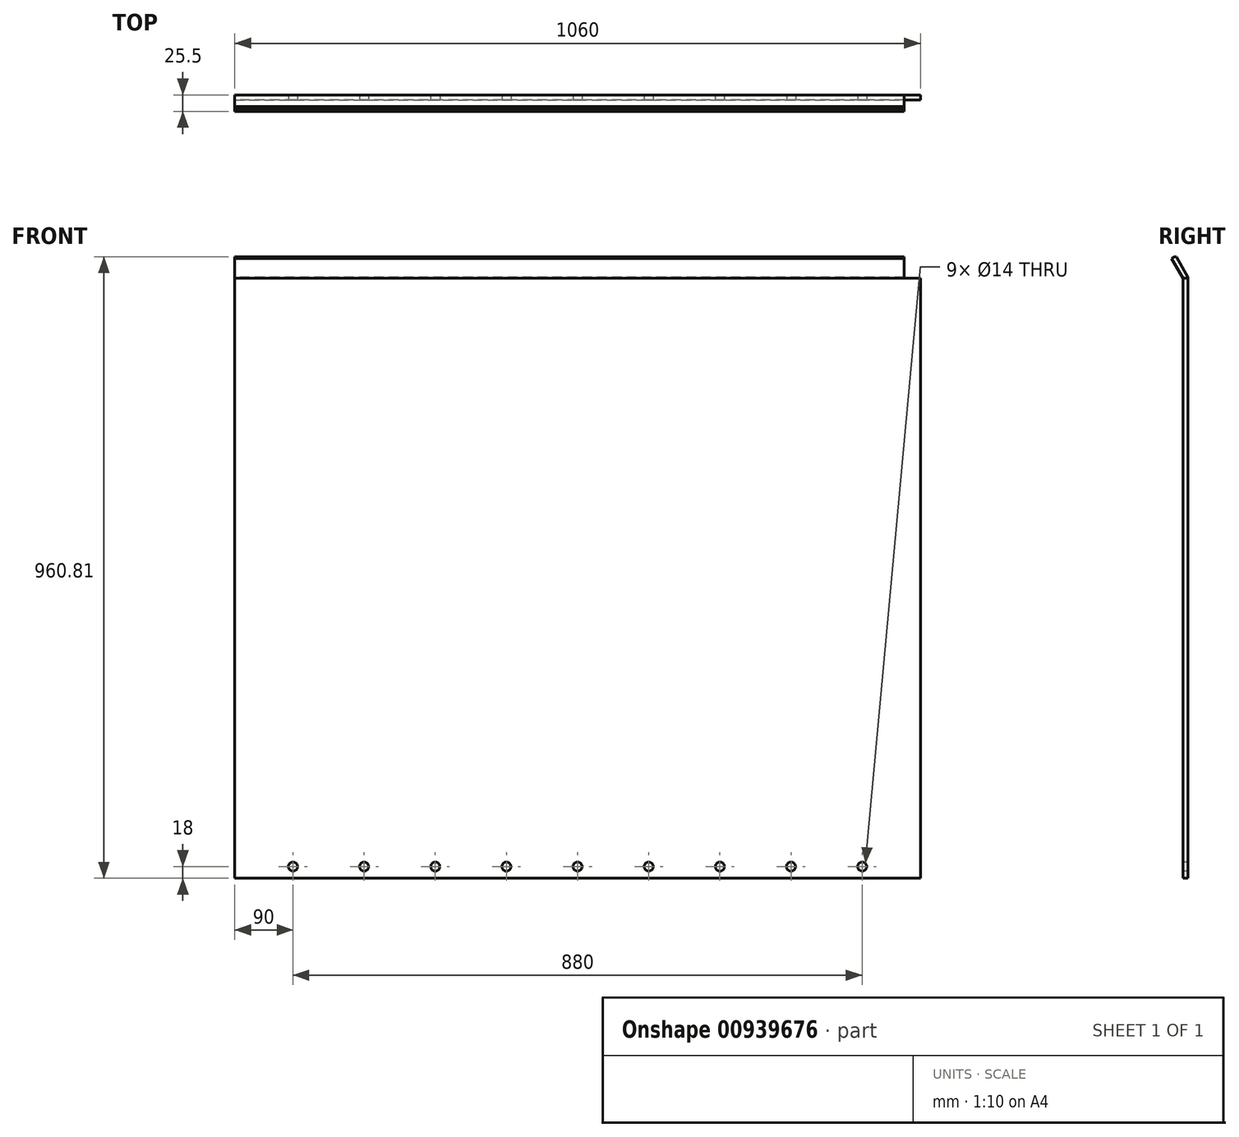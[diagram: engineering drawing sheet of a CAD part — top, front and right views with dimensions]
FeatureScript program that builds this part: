
annotation { "Feature Type Name" : "Feature", "Feature Type Description" : "" }
export const myFeature = defineFeature(function(context is Context, id is Id, definition is map)
    precondition{}
    {
        {
            var Q0;
            Q0=qCreatedBy(makeId("Right.planeOp"),FACE);
            var sketch = newSketch(context, id + "F0", { "sketchPlane" : qUnion([Q0])});
            skLineSegment(sketch, "E0", {"start": v(0, 0) * mm, "end": v(0, 940) * mm});
            skLineSegment(sketch, "E1", {"start": v(0, 0) * mm, "end": v(-6.47, -24.15) * mm});
            skLineSegment(sketch, "E2", {"start": v(0, 940) * mm, "end": v(-17.5, 970.31) * mm});
            skLineSegment(sketch, "E3.0", {"start": v(5, -0.66) * mm, "end": v(-1.64, -25.44) * mm});
            skLineSegment(sketch, "E3.1", {"start": v(5, -0.66) * mm, "end": v(5, 941.34) * mm});
            skLineSegment(sketch, "E3.2", {"start": v(5, 941.34) * mm, "end": v(-13.17, 972.81) * mm});
            skLineSegment(sketch, "E4", {"start": v(-1.64, -25.44) * mm, "end": v(-6.47, -24.15) * mm});
            skLineSegment(sketch, "E5", {"start": v(-13.17, 972.81) * mm, "end": v(-17.5, 970.31) * mm});
            skSolve(sketch);
        }
        {
            var Q0;
            Q0=makeQuery(id+"F0.imprint","IMPRINT",FACE,{"disambiguationData":[TD([[makeQuery(id+"F0.imprint","IMPRINT",EDGE,{"derivedFrom":sQuery(id+"F0.wireOp",EDGE,"E0")}),-1.0]])]});
            extrude(context, id + "F1", {"entities" : qUnion([Q0]), "endBound" : BoundingType.SYMMETRIC, "depth" : 1060 * mm, "offsetDistance" : 25 * mm});
        }
        {
            var Q0;
            Q0=makeQuery(id+"F1.opExtrude","CAP_FACE",FACE,{"disambiguationData":[OSD([sQuery(id+"F0.wireOp",EDGE,"E0"),sQuery(id+"F0.wireOp",EDGE,"E1"),sQuery(id+"F0.wireOp",EDGE,"E2"),sQuery(id+"F0.wireOp",EDGE,"E3.0"),sQuery(id+"F0.wireOp",EDGE,"E3.1"),sQuery(id+"F0.wireOp",EDGE,"E3.2"),sQuery(id+"F0.wireOp",EDGE,"E4"),sQuery(id+"F0.wireOp",EDGE,"E5")])],"isStart":false});
            var sketch = newSketch(context, id + "F2", { "sketchPlane" : qUnion([Q0])});
            skLineSegment(sketch, "E6", {"start": v(0, 940) * mm, "end": v(5, 940) * mm});
            skLineSegment(sketch, "E7", {"start": v(5, 940) * mm, "end": v(5, 941.34) * mm});
            skLineSegment(sketch, "E8", {"start": v(5, 941.34) * mm, "end": v(-13.17, 972.81) * mm});
            skLineSegment(sketch, "E9", {"start": v(-13.17, 972.81) * mm, "end": v(-17.5, 970.31) * mm});
            skLineSegment(sketch, "E10", {"start": v(-17.5, 970.31) * mm, "end": v(0, 940) * mm});
            skLineSegment(sketch, "E11", {"start": v(-6.47, -24.15) * mm, "end": v(-1.64, -25.44) * mm});
            skLineSegment(sketch, "E12", {"start": v(-1.64, -25.44) * mm, "end": v(5, -0.66) * mm});
            skLineSegment(sketch, "E13", {"start": v(5, -0.66) * mm, "end": v(5, 0) * mm});
            skLineSegment(sketch, "E14", {"start": v(5, 0) * mm, "end": v(0, 0) * mm});
            skLineSegment(sketch, "E15", {"start": v(0, 0) * mm, "end": v(-6.47, -24.15) * mm});
            skSolve(sketch);
        }
        {
            var Q0;
            Q0=makeQuery(id+"F2.imprint","IMPRINT",FACE,{"disambiguationData":[TD([[makeQuery(id+"F2.imprint","IMPRINT",EDGE,{"derivedFrom":sQuery(id+"F2.wireOp",EDGE,"E11")}),-1.0]])]});
            var Q1;
            Q1=makeQuery(id+"F2.imprint","IMPRINT",FACE,{"disambiguationData":[TD([[makeQuery(id+"F2.imprint","IMPRINT",EDGE,{"derivedFrom":sQuery(id+"F2.wireOp",EDGE,"E6")}),1.0]])]});
            extrude(context, id + "F3", {"entities" : qUnion([Q0, Q1]), "operationType" : NewBodyOperationType.REMOVE, "oppositeDirection" : true, "depth" : 25 * mm, "offsetDistance" : 25 * mm});
        }
        {
            var Q0;
            Q0=makeQuery(id+"F1.opExtrude","SWEPT_FACE",FACE,{"disambiguationData":[OSD([sQuery(id+"F0.wireOp",EDGE,"E0")])]});
            var sketch = newSketch(context, id + "F4", { "sketchPlane" : qUnion([Q0])});
            skCircle(sketch, "E16", {"center": v(0, 30) * mm, "radius": 7 * mm});
            skCircle(sketch, "E17.1.0.0", {"center": v(110, 30) * mm, "radius": 7 * mm});
            skCircle(sketch, "E17.2.0.0", {"center": v(220, 30) * mm, "radius": 7 * mm});
            skCircle(sketch, "E17.3.0.0", {"center": v(330, 30) * mm, "radius": 7 * mm});
            skCircle(sketch, "E17.4.0.0", {"center": v(440, 30) * mm, "radius": 7 * mm});
            skLineSegment(sketch, "E17.direction1", {"start": v(0, 30) * mm, "end": v(110, 30) * mm, "construction": true});
            skCircle(sketch, "E18.MirrorC", {"center": v(-110, 30) * mm, "radius": 7 * mm});
            skCircle(sketch, "E19.MirrorC", {"center": v(-220, 30) * mm, "radius": 7 * mm});
            skCircle(sketch, "E20.MirrorC", {"center": v(-330, 30) * mm, "radius": 7 * mm});
            skCircle(sketch, "E21.MirrorC", {"center": v(-440, 30) * mm, "radius": 7 * mm});
            skSolve(sketch);
        }
        {
            var Q0;
            Q0=qSketchRegion(id+"F4",true);
            extrude(context, id + "F5", {"entities" : qUnion([Q0]), "operationType" : NewBodyOperationType.REMOVE, "endBound" : BoundingType.THROUGH_ALL, "oppositeDirection" : true, "depth" : 25 * mm, "offsetDistance" : 25 * mm});
        }
        {
            var Q0;
            Q0=makeQuery(id+"F1.opExtrude","CAP_FACE",FACE,{"disambiguationData":[OSD([sQuery(id+"F0.wireOp",EDGE,"E0"),sQuery(id+"F0.wireOp",EDGE,"E1"),sQuery(id+"F0.wireOp",EDGE,"E2"),sQuery(id+"F0.wireOp",EDGE,"E3.0"),sQuery(id+"F0.wireOp",EDGE,"E3.1"),sQuery(id+"F0.wireOp",EDGE,"E3.2"),sQuery(id+"F0.wireOp",EDGE,"E4"),sQuery(id+"F0.wireOp",EDGE,"E5")])],"isStart":false});
            var sketch = newSketch(context, id + "F6", { "sketchPlane" : qUnion([Q0])});
            skLineSegment(sketch, "E22", {"start": v(0, 0) * mm, "end": v(0, 12) * mm});
            skLineSegment(sketch, "E23", {"start": v(0, 12) * mm, "end": v(5, 12) * mm});
            skLineSegment(sketch, "E24", {"start": v(5, 12) * mm, "end": v(5, -0.66) * mm});
            skLineSegment(sketch, "E25", {"start": v(5, -0.66) * mm, "end": v(-1.64, -25.44) * mm});
            skLineSegment(sketch, "E26", {"start": v(-1.64, -25.44) * mm, "end": v(-6.47, -24.15) * mm});
            skLineSegment(sketch, "E27", {"start": v(-6.47, -24.15) * mm, "end": v(0, 0) * mm});
            skSolve(sketch);
        }
        {
            var Q0;
            Q0 = qSketchRegion(id + "F6", true);
            extrude(context, id + "F7", {"entities" : qUnion([Q0]), "operationType" : NewBodyOperationType.REMOVE, "endBound" : BoundingType.THROUGH_ALL, "oppositeDirection" : true, "depth" : 25 * mm, "offsetDistance" : 25 * mm});
        }
        {
            var Q0;
            Q0=makeQuery(id+"F1.opExtrude","SWEPT_FACE",FACE,{"disambiguationData":[OSD([sQuery(id+"F0.wireOp",EDGE,"E3.1")])]});
            var Q1;
            Q1=makeQuery(id+"F1.opExtrude","SWEPT_FACE",FACE,{"disambiguationData":[OSD([sQuery(id+"F0.wireOp",EDGE,"E3.2")])]});
            extrude(context, id + "F8", {"entities" : qUnion([Q0, Q1]), "operationType" : NewBodyOperationType.ADD, "depth" : 3 * mm, "offsetDistance" : 25 * mm});
        }
    });
